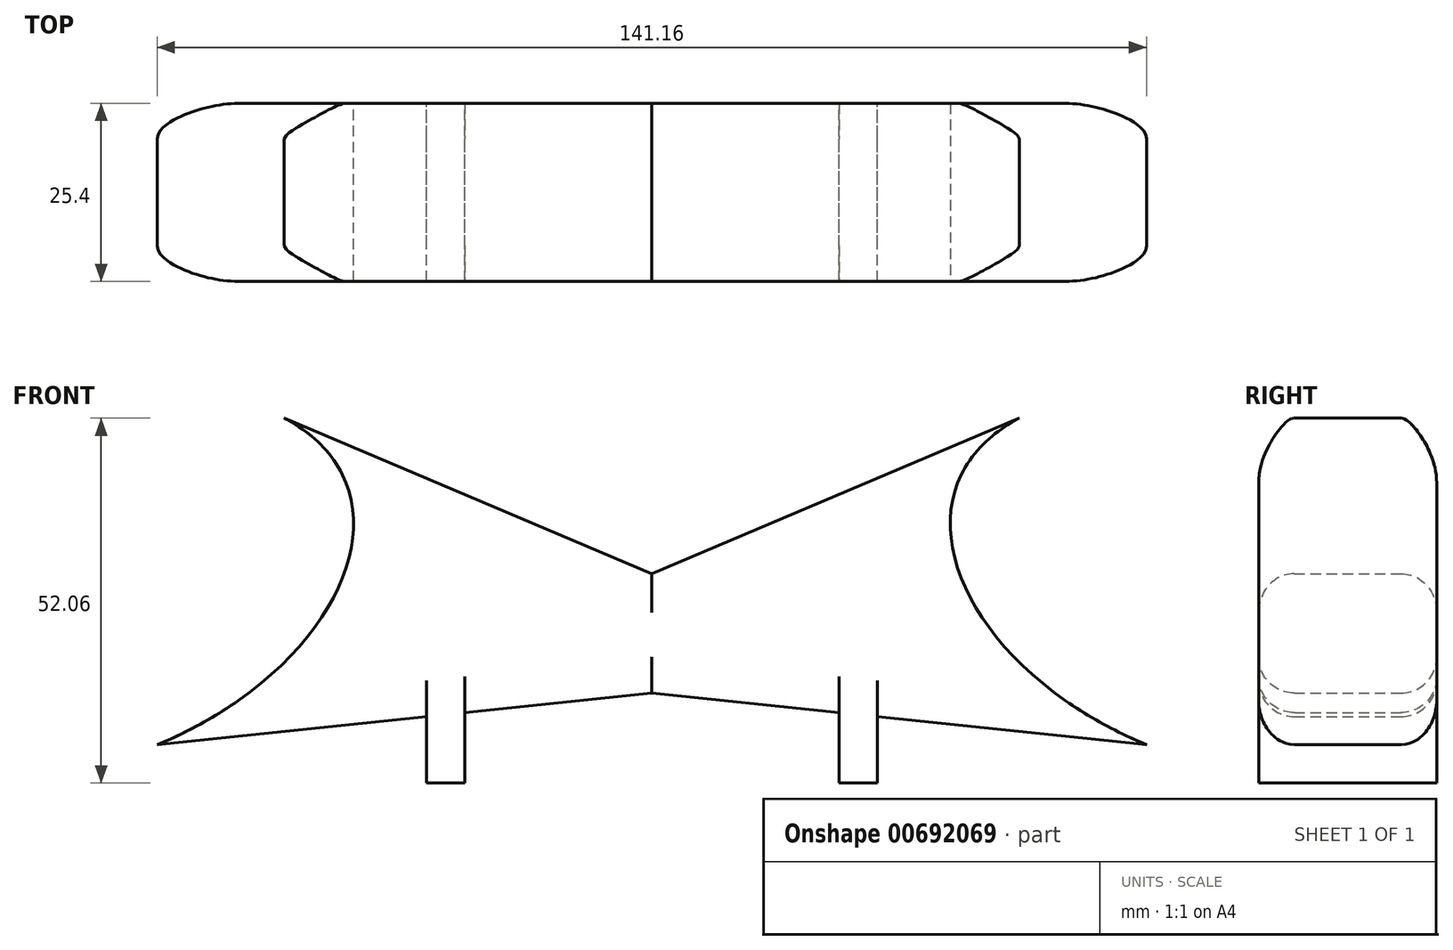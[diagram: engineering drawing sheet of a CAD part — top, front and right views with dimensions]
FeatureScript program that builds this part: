
annotation { "Feature Type Name" : "Feature", "Feature Type Description" : "" }
export const myFeature = defineFeature(function(context is Context, id is Id, definition is map)
    precondition{}
    {
        {
            var Q0;
            Q0=qCreatedBy(makeId("Front.planeOp"),FACE);
            var sketch = newSketch(context, id + "F0", { "sketchPlane" : qUnion([Q0])});
            skLineSegment(sketch, "E0", {"start": v(0, 13.13) * mm, "end": v(-52.45, 35.33) * mm});
            skLineSegment(sketch, "E1.MirrorCS", {"start": v(0, 13.13) * mm, "end": v(52.45, 35.33) * mm});
            skLineSegment(sketch, "E2", {"start": v(0, -3.88) * mm, "end": v(-70.58, -11.28) * mm});
            skLineSegment(sketch, "E3.MirrorCS", {"start": v(0, -3.88) * mm, "end": v(70.58, -11.28) * mm});
            skFitSpline(sketch, "E4", {"points": [v(-52.45, 35.33) * mm, v(-70.58, -11.28) * mm], "startDerivative": vector(57.72, -30.52) * mm, "endDerivative": vector(-81.03, -33.85) * mm});
            skFitSpline(sketch, "E5.MirrorCS", {"points": [v(52.45, 35.33) * mm, v(70.58, -11.28) * mm], "startDerivative": vector(-57.72, -30.52) * mm, "endDerivative": vector(81.03, -33.85) * mm});
            skLineSegment(sketch, "E6", {"start": v(-32.16, -7.26) * mm, "end": v(-32.16, -16.73) * mm});
            skLineSegment(sketch, "E7", {"start": v(-32.16, -16.73) * mm, "end": v(-26.7, -16.73) * mm});
            skLineSegment(sketch, "E8", {"start": v(-26.7, -16.73) * mm, "end": v(-26.7, -6.68) * mm});
            skLineSegment(sketch, "E9.MirrorCS", {"start": v(26.7, -16.73) * mm, "end": v(26.7, -6.68) * mm});
            skLineSegment(sketch, "E10.MirrorCS", {"start": v(32.16, -7.26) * mm, "end": v(32.16, -16.73) * mm});
            skLineSegment(sketch, "E11.MirrorCS", {"start": v(32.16, -16.73) * mm, "end": v(26.7, -16.73) * mm});
            skSolve(sketch);
        }
        {
            var Q0;
            Q0=makeQuery(id+"F0.imprint","IMPRINT",FACE,{"disambiguationData":[TD([[makeQuery(id+"F0.imprint","IMPRINT",EDGE,{"derivedFrom":sQuery(id+"F0.wireOp",EDGE,"E0")}),1.0]])]});
            extrude(context, id + "F1", {"entities" : qUnion([Q0]), "depth" : 12.7 * mm, "offsetDistance" : 25.4 * mm});
        }
        {
            var Q0;
            Q0 = qSketchRegion(id + "F0", true);
            extrude(context, id + "F2", {"entities" : qUnion([Q0]), "operationType" : NewBodyOperationType.ADD, "depth" : 25.4 * mm, "offsetDistance" : 25.4 * mm});
        }
        {
            var Q0;
            Q0=makeQuery(id+"F2.opExtrude","CAP_EDGE",EDGE,{"disambiguationData":[OSD([sQuery(id+"F0.wireOp",EDGE,"E0")])],"isStart":false});
            var Q1;
            Q1=makeQuery(id+"F2.opExtrude","CAP_EDGE",EDGE,{"disambiguationData":[OSD([sQuery(id+"F0.wireOp",EDGE,"E1.MirrorCS")])],"isStart":false});
            var Q2;
            Q2=makeQuery(id+"F1.opExtrude","CAP_EDGE",EDGE,{"disambiguationData":[OSD([sQuery(id+"F0.wireOp",EDGE,"E0")])],"isStart":true});
            var Q3;
            Q3=makeQuery(id+"F1.opExtrude","CAP_EDGE",EDGE,{"disambiguationData":[OSD([sQuery(id+"F0.wireOp",EDGE,"E1.MirrorCS")])],"isStart":true});
            var Q4;
            {var subQ0=sQuery(id+"F0.wireOp",EDGE,"E3.MirrorCS");Q4=makeQuery(id+"F2.opExtrude","CAP_EDGE",EDGE,{"disambiguationData":[OSD([subQ0]),TDD([makeQuery(id+"F0.imprint","IMPRINT",EDGE,{"disambiguationData":[TD([[makeQuery(id+"F0.imprint","INTERSECT",VERTEX,{"derivedFrom":[subQ0,sQuery(id+"F0.wireOp",EDGE,"E5.MirrorCS")]}),1.0]])],"derivedFrom":subQ0})])],"isStart":false});}
            var Q5;
            {var subQ0=sQuery(id+"F0.wireOp",EDGE,"E3.MirrorCS");Q5=makeQuery(id+"F2.opExtrude","CAP_EDGE",EDGE,{"disambiguationData":[OSD([subQ0]),TDD([makeQuery(id+"F0.imprint","IMPRINT",EDGE,{"disambiguationData":[TD([[makeQuery(id+"F0.imprint","INTERSECT",VERTEX,{"derivedFrom":[sQuery(id+"F0.wireOp",EDGE,"E2"),subQ0]}),-1.0]])],"derivedFrom":subQ0})])],"isStart":false});}
            var Q6;
            {var subQ0=sQuery(id+"F0.wireOp",EDGE,"E2");Q6=makeQuery(id+"F2.opExtrude","CAP_EDGE",EDGE,{"disambiguationData":[OSD([subQ0]),TDD([makeQuery(id+"F0.imprint","IMPRINT",EDGE,{"disambiguationData":[TD([[makeQuery(id+"F0.imprint","INTERSECT",VERTEX,{"derivedFrom":[subQ0,sQuery(id+"F0.wireOp",EDGE,"E3.MirrorCS")]}),-1.0]])],"derivedFrom":subQ0})])],"isStart":false});}
            var Q7;
            {var subQ0=sQuery(id+"F0.wireOp",EDGE,"E2");Q7=makeQuery(id+"F2.opExtrude","CAP_EDGE",EDGE,{"disambiguationData":[OSD([subQ0]),TDD([makeQuery(id+"F0.imprint","IMPRINT",EDGE,{"disambiguationData":[TD([[makeQuery(id+"F0.imprint","INTERSECT",VERTEX,{"derivedFrom":[subQ0,sQuery(id+"F0.wireOp",EDGE,"E4")]}),1.0]])],"derivedFrom":subQ0})])],"isStart":false});}
            var Q8;
            {var subQ0=sQuery(id+"F0.wireOp",EDGE,"E5.MirrorCS");var subQ2=sQuery(id+"F0.wireOp",EDGE,"E3.MirrorCS");Q8=makeQuery(id+"F2.boolean.opBoolean","SPLIT",EDGE,{"disambiguationData":[topologyDisambiguationEdgeConnected([makeQuery(id+"F2.opExtrude","SWEPT_FACE",FACE,{"disambiguationData":[OSD([subQ2]),TDD([makeQuery(id+"F0.imprint","IMPRINT",EDGE,{"disambiguationData":[TD([[makeQuery(id+"F0.imprint","INTERSECT",VERTEX,{"derivedFrom":[subQ2,subQ0]}),1.0]])],"derivedFrom":subQ2})])]})])],"derivedFrom":makeQuery(id+"F1.opExtrude","CAP_EDGE",EDGE,{"disambiguationData":[OSD([subQ2])],"isStart":true})});}
            var Q9;
            {var subQ2=sQuery(id+"F0.wireOp",EDGE,"E3.MirrorCS");var subQ3=sQuery(id+"F0.wireOp",EDGE,"E2");Q9=makeQuery(id+"F2.boolean.opBoolean","SPLIT",EDGE,{"disambiguationData":[topologyDisambiguationEdgeConnected([makeQuery(id+"F2.opExtrude","SWEPT_FACE",FACE,{"disambiguationData":[OSD([subQ2]),TDD([makeQuery(id+"F0.imprint","IMPRINT",EDGE,{"disambiguationData":[TD([[makeQuery(id+"F0.imprint","INTERSECT",VERTEX,{"derivedFrom":[subQ3,subQ2]}),-1.0]])],"derivedFrom":subQ2})])]})])],"derivedFrom":makeQuery(id+"F1.opExtrude","CAP_EDGE",EDGE,{"disambiguationData":[OSD([subQ2])],"isStart":true})});}
            var Q10;
            {var subQ2=sQuery(id+"F0.wireOp",EDGE,"E3.MirrorCS");var subQ3=sQuery(id+"F0.wireOp",EDGE,"E2");Q10=makeQuery(id+"F2.boolean.opBoolean","SPLIT",EDGE,{"disambiguationData":[topologyDisambiguationEdgeConnected([makeQuery(id+"F2.opExtrude","SWEPT_FACE",FACE,{"disambiguationData":[OSD([subQ3]),TDD([makeQuery(id+"F0.imprint","IMPRINT",EDGE,{"disambiguationData":[TD([[makeQuery(id+"F0.imprint","INTERSECT",VERTEX,{"derivedFrom":[subQ3,subQ2]}),-1.0]])],"derivedFrom":subQ3})])]})])],"derivedFrom":makeQuery(id+"F1.opExtrude","CAP_EDGE",EDGE,{"disambiguationData":[OSD([subQ3])],"isStart":true})});}
            var Q11;
            {var subQ1=sQuery(id+"F0.wireOp",EDGE,"E4");var subQ3=sQuery(id+"F0.wireOp",EDGE,"E2");Q11=makeQuery(id+"F2.boolean.opBoolean","SPLIT",EDGE,{"disambiguationData":[topologyDisambiguationEdgeConnected([makeQuery(id+"F2.opExtrude","SWEPT_FACE",FACE,{"disambiguationData":[OSD([subQ3]),TDD([makeQuery(id+"F0.imprint","IMPRINT",EDGE,{"disambiguationData":[TD([[makeQuery(id+"F0.imprint","INTERSECT",VERTEX,{"derivedFrom":[subQ3,subQ1]}),1.0]])],"derivedFrom":subQ3})])]})])],"derivedFrom":makeQuery(id+"F1.opExtrude","CAP_EDGE",EDGE,{"disambiguationData":[OSD([subQ3])],"isStart":true})});}
            fillet(context, id + "F3", {"entities" : qUnion([Q0, Q1, Q2, Q3, Q4, Q5, Q6, Q7, Q8, Q9, Q10, Q11]), "radius" : 5.08 * mm, "tangentPropagation" : true, "allowEdgeOverflow" : false});
        }
        {
            var Q0;
            Q0=makeQuery(id+"F2.opExtrude","CAP_FACE",FACE,{"disambiguationData":[OSD([sQuery(id+"F0.wireOp",EDGE,"E0"),sQuery(id+"F0.wireOp",EDGE,"E1.MirrorCS"),sQuery(id+"F0.wireOp",EDGE,"E2"),sQuery(id+"F0.wireOp",EDGE,"E3.MirrorCS"),sQuery(id+"F0.wireOp",EDGE,"E4"),sQuery(id+"F0.wireOp",EDGE,"E5.MirrorCS"),sQuery(id+"F0.wireOp",EDGE,"E6"),sQuery(id+"F0.wireOp",EDGE,"E7"),sQuery(id+"F0.wireOp",EDGE,"E8"),sQuery(id+"F0.wireOp",EDGE,"E9.MirrorCS"),sQuery(id+"F0.wireOp",EDGE,"E10.MirrorCS"),sQuery(id+"F0.wireOp",EDGE,"E11.MirrorCS")])],"isStart":false});
            var sketch = newSketch(context, id + "F4", { "sketchPlane" : qUnion([Q0])});
            skLineSegment(sketch, "E12.bottom", {"start": v(-12.16, 7.15) * mm, "end": v(12.57, 7.15) * mm});
            skLineSegment(sketch, "E12.top", {"start": v(-12.16, 2.23) * mm, "end": v(12.57, 2.23) * mm});
            skLineSegment(sketch, "E12.left", {"start": v(-12.16, 7.15) * mm, "end": v(-12.16, 2.23) * mm});
            skLineSegment(sketch, "E12.right", {"start": v(12.57, 7.15) * mm, "end": v(12.57, 2.23) * mm});
            skText(sketch, "E13", { "text": "7:43 FRI", "fontName": "OpenSans-Regular.ttf"});
            const initialGuessF4  = {"E13": [-0.01216, 0.00223, 1, 0, 0.00492]};
            skSetInitialGuess(sketch, initialGuessF4);
            skSolve(sketch);
        }
        {
            var Q0;
            {var subQ8=sQuery(id+"F4.wireOp",EDGE,"E12.left");Q0=makeQuery(id+"F4.imprint","IMPRINT",FACE,{"disambiguationData":[TD([[makeQuery(id+"F4.imprint","IMPRINT",EDGE,{"derivedFrom":subQ8}),1.0]])]});}
            var Q1;
            {var subQ9=sQuery(id+"F4.wireOp",EDGE,"E12.right");Q1=makeQuery(id+"F4.imprint","IMPRINT",FACE,{"disambiguationData":[TD([[makeQuery(id+"F4.imprint","IMPRINT",EDGE,{"derivedFrom":subQ9}),-1.0]])]});}
            extrude(context, id + "F5", {"entities" : qUnion([Q0, Q1]), "operationType" : NewBodyOperationType.ADD, "oppositeDirection" : true, "depth" : 19.8 * mm, "offsetDistance" : 25.4 * mm});
        }
    });
